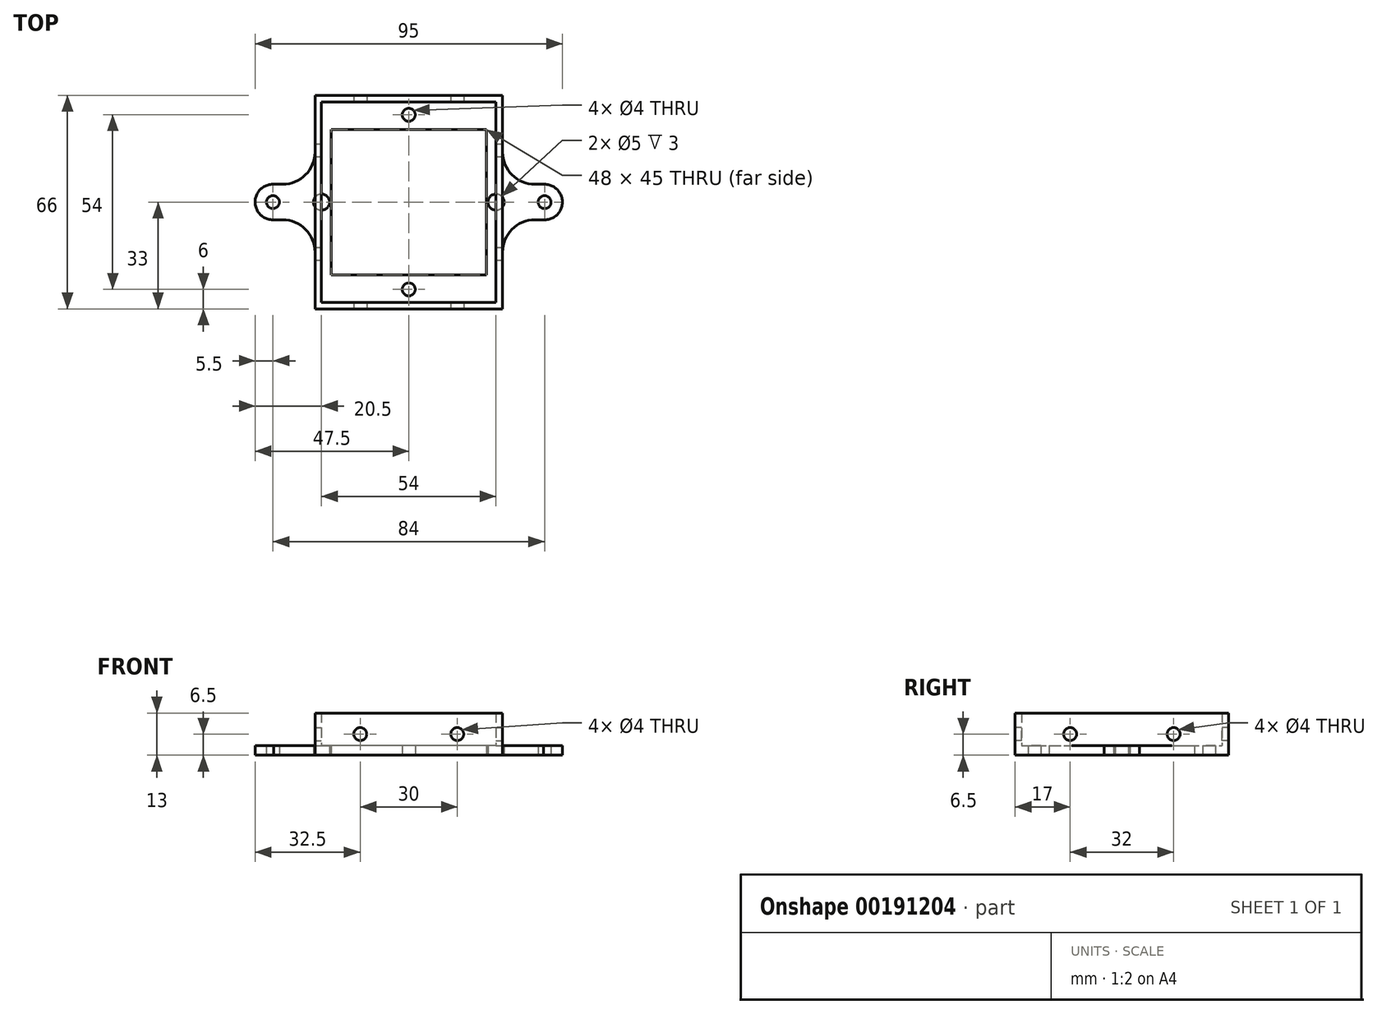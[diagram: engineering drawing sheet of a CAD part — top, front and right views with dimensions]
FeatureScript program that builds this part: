
annotation { "Feature Type Name" : "Feature", "Feature Type Description" : "" }
export const myFeature = defineFeature(function(context is Context, id is Id, definition is map)
    precondition{}
    {
        {
            var Q0;
            Q0=qCreatedBy(makeId("Top.planeOp"),FACE);
            var sketch = newSketch(context, id + "F0", { "sketchPlane" : qUnion([Q0])});
            skLineSegment(sketch, "E0.bottom", {"start": v(29, -33) * mm, "end": v(-29, -33) * mm});
            skLineSegment(sketch, "E0.top", {"start": v(29, 33) * mm, "end": v(-29, 33) * mm});
            skLineSegment(sketch, "E0.left", {"start": v(29, -33) * mm, "end": v(29, -15.5) * mm});
            skLineSegment(sketch, "E0.right", {"start": v(-29, -33) * mm, "end": v(-29, -15.5) * mm});
            skPoint(sketch, "E0.middle", {"position": v(0, 0) * mm});
            skCircle(sketch, "E1", {"center": v(0, 27) * mm, "radius": 2 * mm});
            skCircle(sketch, "E2", {"center": v(0, -27) * mm, "radius": 2 * mm});
            skCircle(sketch, "E3", {"center": v(-42, 0) * mm, "radius": 2 * mm});
            skPoint(sketch, "E3.centerSnap0", {"position": v(29, 0) * mm});
            skCircle(sketch, "E4", {"center": v(42, 0) * mm, "radius": 2 * mm});
            skArc(sketch, "E5", {"start": v(-42, 5.5) * mm, "mid": v(-47.5, -0.15) * mm, "end": v(-41.7, -5.5) * mm});
            skArc(sketch, "E6", {"start": v(41.7, -5.5) * mm, "mid": v(47.5, -0.15) * mm, "end": v(42, 5.5) * mm});
            skLineSegment(sketch, "E7", {"start": v(-42, 5.5) * mm, "end": v(-39, 5.5) * mm});
            skLineSegment(sketch, "E8", {"start": v(41.7, -5.5) * mm, "end": v(39, -5.5) * mm});
            skLineSegment(sketch, "E9.trimOffspring", {"start": v(39, 5.5) * mm, "end": v(42, 5.5) * mm});
            skLineSegment(sketch, "E10.trimOffspring", {"start": v(-39, -5.5) * mm, "end": v(-41.7, -5.5) * mm});
            skLineSegment(sketch, "E11.trimOffspring", {"start": v(-29, 15.5) * mm, "end": v(-29, 33) * mm});
            skLineSegment(sketch, "E12.trimOffspring", {"start": v(29, 15.5) * mm, "end": v(29, 33) * mm});
            skPoint(sketch, "E13.visualSharp", {"position": v(-29, -5.5) * mm});
            skArc(sketch, "E13.filletArc", {"start": v(-29, -15.5) * mm, "mid": v(-31.93, -8.42) * mm, "end": v(-39, -5.5) * mm});
            skPoint(sketch, "E14.visualSharp", {"position": v(-29, 5.5) * mm});
            skArc(sketch, "E14.filletArc", {"start": v(-39, 5.5) * mm, "mid": v(-31.93, 8.43) * mm, "end": v(-29, 15.5) * mm});
            skPoint(sketch, "E15.visualSharp", {"position": v(29, 5.5) * mm});
            skArc(sketch, "E15.filletArc", {"start": v(29, 15.5) * mm, "mid": v(31.93, 8.43) * mm, "end": v(39, 5.5) * mm});
            skPoint(sketch, "E16.visualSharp", {"position": v(29, -5.5) * mm});
            skArc(sketch, "E16.filletArc", {"start": v(39, -5.5) * mm, "mid": v(31.93, -8.42) * mm, "end": v(29, -15.5) * mm});
            skLineSegment(sketch, "E17.bottom", {"start": v(24, -22.5) * mm, "end": v(-24, -22.5) * mm});
            skLineSegment(sketch, "E17.top", {"start": v(24, 22.5) * mm, "end": v(-24, 22.5) * mm});
            skLineSegment(sketch, "E17.left", {"start": v(24, -22.5) * mm, "end": v(24, 22.5) * mm});
            skLineSegment(sketch, "E17.right", {"start": v(-24, -22.5) * mm, "end": v(-24, 22.5) * mm});
            skCircle(sketch, "E18", {"center": v(27, 0) * mm, "radius": 2.5 * mm});
            skCircle(sketch, "E19", {"center": v(-27, 0) * mm, "radius": 2.5 * mm});
            skSolve(sketch);
        }
        {
            var Q0;
            Q0 = qSketchRegion(id + "F0", true);
            extrude(context, id + "F1", {"entities" : qUnion([Q0]), "depth" : 3 * mm});
        }
        {
            var Q0;
            Q0=makeQuery(id+"F1.opExtrude","CAP_FACE",FACE,{"disambiguationData":[OSD([sQuery(id+"F0.wireOp",EDGE,"E0.bottom"),sQuery(id+"F0.wireOp",EDGE,"E0.top"),sQuery(id+"F0.wireOp",EDGE,"E0.left"),sQuery(id+"F0.wireOp",EDGE,"E0.right"),sQuery(id+"F0.wireOp",EDGE,"E1"),sQuery(id+"F0.wireOp",EDGE,"E2"),sQuery(id+"F0.wireOp",EDGE,"E3"),sQuery(id+"F0.wireOp",EDGE,"E4"),sQuery(id+"F0.wireOp",EDGE,"E5"),sQuery(id+"F0.wireOp",EDGE,"E6"),sQuery(id+"F0.wireOp",EDGE,"E7"),sQuery(id+"F0.wireOp",EDGE,"E8"),sQuery(id+"F0.wireOp",EDGE,"E9.trimOffspring"),sQuery(id+"F0.wireOp",EDGE,"E10.trimOffspring"),sQuery(id+"F0.wireOp",EDGE,"E11.trimOffspring"),sQuery(id+"F0.wireOp",EDGE,"E12.trimOffspring"),sQuery(id+"F0.wireOp",EDGE,"E13.filletArc"),sQuery(id+"F0.wireOp",EDGE,"E14.filletArc"),sQuery(id+"F0.wireOp",EDGE,"E15.filletArc"),sQuery(id+"F0.wireOp",EDGE,"E16.filletArc")])],"isStart":false});
            var sketch = newSketch(context, id + "F2", { "sketchPlane" : qUnion([Q0])});
            skLineSegment(sketch, "E20.bottom", {"start": v(29, -33) * mm, "end": v(-29, -33) * mm});
            skLineSegment(sketch, "E20.top", {"start": v(29, 33) * mm, "end": v(-29, 33) * mm});
            skLineSegment(sketch, "E20.left", {"start": v(29, -33) * mm, "end": v(29, 33) * mm});
            skLineSegment(sketch, "E20.right", {"start": v(-29, -33) * mm, "end": v(-29, 33) * mm});
            skPoint(sketch, "E20.middle", {"position": v(0, 0) * mm});
            skLineSegment(sketch, "E21.bottom", {"start": v(27, -31) * mm, "end": v(-27, -31) * mm});
            skLineSegment(sketch, "E21.top", {"start": v(27, 31) * mm, "end": v(-27, 31) * mm});
            skLineSegment(sketch, "E21.left", {"start": v(27, -31) * mm, "end": v(27, 31) * mm});
            skLineSegment(sketch, "E21.right", {"start": v(-27, -31) * mm, "end": v(-27, 31) * mm});
            skSolve(sketch);
        }
        {
            var Q0;
            Q0 = qSketchRegion(id + "F2", true);
            extrude(context, id + "F3", {"entities" : qUnion([Q0]), "operationType" : NewBodyOperationType.ADD, "depth" : 10 * mm});
        }
        {
            var Q0;
            Q0=makeQuery(id+"F3.boolean.opBoolean","MERGE",FACE,{"derivedFrom":[makeQuery(id+"F1.opExtrude","SWEPT_FACE",FACE,{"disambiguationData":[OSD([sQuery(id+"F0.wireOp",EDGE,"E0.bottom")])]}),makeQuery(id+"F3.opExtrude","SWEPT_FACE",FACE,{"disambiguationData":[OSD([sQuery(id+"F2.wireOp",EDGE,"E20.bottom")])]})]});
            var sketch = newSketch(context, id + "F4", { "sketchPlane" : qUnion([Q0])});
            skCircle(sketch, "E22", {"center": v(-15, 6.5) * mm, "radius": 2 * mm});
            skPoint(sketch, "E22.centerSnap0", {"position": v(-29, 6.5) * mm});
            skCircle(sketch, "E23", {"center": v(15, 6.5) * mm, "radius": 2 * mm});
            skSolve(sketch);
        }
        {
            var Q0;
            Q0 = qSketchRegion(id + "F4", true);
            extrude(context, id + "F5", {"entities" : qUnion([Q0]), "operationType" : NewBodyOperationType.REMOVE, "oppositeDirection" : true, "depth" : 150 * mm});
        }
        {
            var Q0;
            Q0=makeQuery(id+"F3.boolean.opBoolean","MERGE",FACE,{"derivedFrom":[makeQuery(id+"F1.opExtrude","SWEPT_FACE",FACE,{"disambiguationData":[OSD([sQuery(id+"F0.wireOp",EDGE,"E0.left")])]}),makeQuery(id+"F1.opExtrude","SWEPT_FACE",FACE,{"disambiguationData":[OSD([sQuery(id+"F0.wireOp",EDGE,"E12.trimOffspring")])]}),makeQuery(id+"F3.opExtrude","SWEPT_FACE",FACE,{"disambiguationData":[OSD([sQuery(id+"F2.wireOp",EDGE,"E20.left")])]})]});
            var sketch = newSketch(context, id + "F6", { "sketchPlane" : qUnion([Q0])});
            skCircle(sketch, "E24", {"center": v(-16, 6.5) * mm, "radius": 2 * mm});
            skPoint(sketch, "E24.centerSnap0", {"position": v(-33, 6.5) * mm});
            skCircle(sketch, "E25", {"center": v(16, 6.5) * mm, "radius": 2 * mm});
            skPoint(sketch, "E25.centerSnap0", {"position": v(33, 6.5) * mm});
            skSolve(sketch);
        }
        {
            var Q0;
            Q0 = qSketchRegion(id + "F6", true);
            extrude(context, id + "F7", {"entities" : qUnion([Q0]), "operationType" : NewBodyOperationType.REMOVE, "oppositeDirection" : true, "depth" : 150 * mm});
        }
    });
